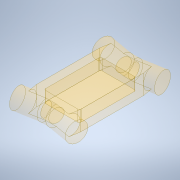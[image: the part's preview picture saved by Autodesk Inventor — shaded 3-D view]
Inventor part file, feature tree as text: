
AUTODESK INVENTOR PART (.ipt)
format: ipt  version: 2020.2 (Build 242310000, 310)  size: 1,997,824 bytes
history: native  units: mm
features: sketch x7, extrude x6, revolve x5, other x5, plane x4, mirror x4
ambient origin geometry x8: Origin, YZ Plane, XZ Plane, XY Plane, X Axis, Y Axis, Z Axis, Center Point
bodies: Solid1 (feature_tree)
feature tree (31):
  sketch  "Sketch1"  dims[d0=1.745329mm d1=1.0mm]
  sketch  "Sketch24"  dims[d12=7.0mm d13=27.0mm]
  sketch  "Sketch_3_division_plane"  dims[d14=3.0mm d15=42.0mm d16=8.0mm d17=260.0mm d24=67.2mm d27=35.453079mm d48=90.0deg d49=67.2mm d50=0.0mm d60=67.2mm d61=0.0mm d63=10.0mm d65=47.2mm d66=0.0mm d67=38.0mm d68=10.0mm d69=23.0mm d77=4.1mm d78=3.3mm d79=90.0deg d80=7.0mm d81=32.0mm d122=12.0mm d128=110.0mm d129=80.0mm d143=56.2mm d144=48.0mm d146=4.0mm d147=2.5mm d148=3.1mm d149=5.0mm d161=6.0mm d162=67.2mm d163=45.2mm d164=0.0mm d165=0.0mm d190=214.629177mm d193=11.0mm d207=1.745329mm d210=90.0deg d211=5.0mm d212=3.1mm d213=2.5mm d215=0.0mm d224=45.2mm d225=29.5mm d226=1.6mm d227=6.981317mm d311=5.0mm d324=6.981317mm d325=0.8mm d326=2.8mm d328=7.0mm d329=6.0mm d338=20.0mm d340=10.0mm d341=10.0mm d343=10.0mm d345=4.0mm d352=2.5mm d353=1.0mm d355=6.981317mm d356=3.0mm d387=1.0mm d388=1.0mm d391=20.0mm d393=10.0mm d394=20.0mm d396=12.0mm d399=4.301042mm d400=5.4mm d401=6.981317mm d405=7.0mm d425=3.0mm d437=3.0mm d438=20.0mm d440=10.0mm d441=10.0mm d443=10.0mm d445=3.0mm d446=4.942038mm d449=10.0mm d451=10.0mm d452=10.0mm d453=5.65mm d456=10.0mm d460=5.0mm d464=40.0mm d468=12.6mm d469=23.783922mm d470=5.0mm d471=14.0mm d480=6.981317mm d481=2.0mm d482=20.0mm d489=20.0mm d491=12.5mm d492=10.0mm d494=10.0mm d496=7.5mm d513=32.767591mm d514=10.0mm d520=234.629177mm d524=8.0mm d525=6.0mm d538=150.0mm d539=4.5mm d542=2.8mm d543=0.6mm d545=2.5mm d546=5.0mm d548=4.5mm d676=2.5mm d709=90.0deg d710=10.0mm d711=0.0mm d715=0.2mm d716=0.0mm d717=85.0mm d718=103.0mm d721=130.0mm d722=4.0mm d723=2.0mm d724=18.0mm d725=361.950606mm d726=175.045532mm d727=2.2mm d728=40.0mm d729=40.0mm d730=135.045532mm d731=346.780847mm d732=285.988171mm d733=90.0deg d734=191.20124mm d736=13.962634mm d737=13.962634mm d738=90.0deg d739=90.0deg d740=400.0mm d741=400.0mm d32=0.5mm d33=0.872665mm d34=0.5mm d35=0.872665mm d472=0.872665mm]
  plane  "Work Plane5"
  plane  "Work Plane4"
  plane  "Work Plane7"
  sketch  "Sketch2"  dims[d3=8.726646mm d4=3.0mm]
  sketch  "Sketch3"  dims[d5=37.0mm d6=2.0mm]
  sketch  "Sketch6"  dims[d7=1.6mm d9=1.6mm]
  sketch  "Sketch11"  dims[d10=42.0mm d11=6.5mm]
  plane  "Work Plane11"
  revolve  "Revolution4"  [1 undecoded]
  extrude  "Extrusion4"  Depth=3.0mm
  extrude  "Extrusion19"  Depth=2.0mm
  extrude  "Extrusion6-body begin"  Depth=1.6mm
  extrude  "Extrusion7_hollow mid body"  Depth=6.5mm
  extrude  "Extrusion48_hollow_front_body"  Depth=27.0mm
  mirror  "Mirror14"
  extrude  "Extrusion50"  Depth=85.0mm
  other  "Thicken81_simulation_compensation"
  mirror  "Mirror15"
  mirror  "Mirror17"
  mirror  "Mirror18"
  other  "Srf8"
  other  "Srf9"
  other  "Srf12"
  other  "Srf13"
  revolve  "RevolutionSrf1"  [1 undecoded]
  revolve  "RevolutionSrf2"  [1 undecoded]
  revolve  "RevolutionSrf4"  [1 undecoded]
  revolve  "RevolutionSrf5"  [1 undecoded]
note: 5 required parameter values undecoded (feature->parameter linkage not recoverable at this tier; creation-order binding heuristic only, values carry confidence <= 0.55)
